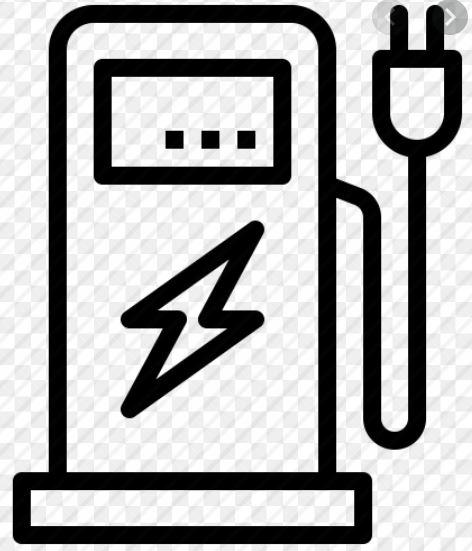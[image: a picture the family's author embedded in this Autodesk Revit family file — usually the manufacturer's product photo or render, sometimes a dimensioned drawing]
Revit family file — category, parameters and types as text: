
# Revit family: Building-RicaricaVeicoliElettrici-GEWISS-JOINON-ICON_PREMIUM-CAVO
name_source: partatom
category: Apparecchi elettrici
units: mm (PartAtom-declared; Revit-internal decimal feet)

## family parameters
Condiviso = No
Host = Superficie
Mantenere orientamento annotazione = Sì
Punto di calcolo locali = Sì
Quota connettore circolare = Usa diametro
Taglio con vuoti quando caricato = No
Tipo di parte = Normale

## types (1)
- Building-RicaricaVeicoliElettrici-GEWISS-JOINON-ICON_PREMIUM-CAVO
    Attivazione ricarica = Accesso Libero, con gestione dinamica dei carichi
    BLOCCO = B=C
    Caratteristiche meccaniche = -
    Codice Electrocod = 2242
    Colore = Grigio scuro
    Connettività: = BLE
    Contatore di energia = Attualmente non presente
    Corrente erogata (max): = 16 Ampere
    Corrente nominale: = 16 Ampere
    DC Leakage check = Si
    Descrizione = JOINON I-CON AUTOSTART BACKLIGHT DLM+BLE 11KW (NO INCASSO) CB
    FORMULA = 1000 mm  [stored 3.28084 ft]
    Grado di protezione = IP55
    Human Interface = LED RGB + Display con slide touch
    IDF = e50fecf7-bc17-4ce4-b331-1b20dbc21f50
    INPUT: = -
    Immagine tipo = ICON_PREMIUM_S.jpg
    L = 155 mm  [stored 0.50853 ft]
    Materiale = Termoplastico (origine Post Industrial)
    Modello = GWJ3313A
    Morsettiera: = 5 x 10 mm²
    N. Prese Tipo 2 = 1
    N.poli = 1
    Numero di prese (tipo) = 1 (connettore Tipo 2 con cavo 5 mt)
    OUTPUT : = -
    POMELLO = bianco
    PRESA = Giallo
    Personalizzabile: = No
    Potenza complessiva: = 11 Chilowatt
    Potenza di ricarica = 11 kW
    Potenza max = 11 Chilowatt
    Produttore = GEWISS S.p.A.
    Prospetto di default = 1219 mm
    Protezione magnetotermica = Attualmente non presente
    Protezioni = DC Leak 6mA
    Resistenza agli urti = IK10
    Riarmo protezioni da remoto = Attualmente non presente
    STRUTTURA = RAL - 7035
    STRUTTURA ALTA = blue
    Segnalazione BACKLIGHT = Si
    Spostamento_S = 1500 mm  [stored 4.92126 ft]
    Temperatura di utilizzo = -25 +50 °C
    Tensione nominale = 400 Volt
    Tensione nominale di isolamento (Ui) = 400 Volt
    Tipo di installazione e montaggio = A parete o su supporto a pavimento
    Tipo di protezione differenziale = Attualmente non presente
    Tipologia Presa: = Tipo 2 mobile con cavo
    Trattamento esterno = No
    URL = https://www.gewiss.com
    VETRO = Vetro
    Versione file RFA = 19.4
    Voltaggio = 0 V
    W = 115 mm  [stored 0.377297 ft]

note: [stored X ft] marks values corroborated as IEEE doubles in the binary element streams (Revit-internal decimal feet)

## geometry (parser evidence)
native form markers: Sweep x2
no freeform markers — native parametric forms only
